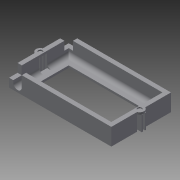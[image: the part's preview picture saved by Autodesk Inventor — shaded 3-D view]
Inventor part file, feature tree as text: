
AUTODESK INVENTOR PART (.ipt)
format: ipt  version: 2014 SP1 (Build 180222100, 222)  size: 205,824 bytes
history: native  units: in
note: dims shown in document units (in); Inventor stores cm internally (conversion verified against a paired STEP export)
features: extrude x9, sketch x9, fillet x1
ambient origin geometry x8: Origin, YZ Plane, XZ Plane, XY Plane, X Axis, Y Axis, Z Axis, Center Point
bodies: Solid1 (feature_tree)
feature tree (19):
  extrude  "Extrusion1"  Depth=0.25in
  extrude  "Extrusion2"  Depth=0.25in
  extrude  "Extrusion3"  Depth=0.5in TaperAngle=0.0deg
  extrude  "Extrusion4"  Depth=0.0625in TaperAngle=0.0deg
  extrude  "Extrusion5"  Depth=0.125in
  extrude  "Extrusion6"  Depth=0.4375in TaperAngle=0.0deg
  extrude  "Extrusion7"  Depth=0.125in
  extrude  "Extrusion8"  Depth=0.4375in TaperAngle=0.0deg
  extrude  "Extrusion9"  Depth=0.25in TaperAngle=0.0deg
  fillet  "Fillet4"  Radius=0.125in
  sketch  "Sketch1"  dims[d1=3.0in d7=0.25in]
  sketch  "Sketch2"  dims[d8=0.25in d9=2.914in]
  sketch  "Sketch3"  dims[d10=1.75in d11=0.5in d12=0.0in]
  sketch  "Sketch4"  dims[d15=0.4375in d16=0.0in d17=0.0625in d18=0.0in]
  sketch  "Sketch5"  dims[d19=0.125in d20=0.125in]
  sketch  "Sketch6"  dims[d21=0.0312in d22=0.0in d23=0.4375in d24=0.0in]
  sketch  "Sketch7"  dims[d25=0.125in d26=0.125in]
  sketch  "Sketch8"  dims[d27=0.0312in d28=0.0in d36=0.4375in d37=0.0in]
  sketch  "Sketch9"  dims[d38=0.4375in d39=0.0in d41=0.25in d42=0.0in d45=0.125in]
